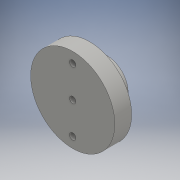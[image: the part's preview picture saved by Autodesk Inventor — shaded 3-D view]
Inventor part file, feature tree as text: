
AUTODESK INVENTOR PART (.ipt)
format: ipt  version: 2016 (Build 200138000, 138)  size: 136,704 bytes
history: native  units: in
note: dims shown in document units (in); Inventor stores cm internally (conversion verified against a paired STEP export)
features: sketch x3, extrude x2, plane x1
ambient origin geometry x8: Origin, YZ Plane, XZ Plane, XY Plane, X Axis, Y Axis, Z Axis, Center Point
bodies: Solid1 (feature_tree)
feature tree (6):
  extrude  "Extrusion1"  Depth=0.2in TaperAngle=0.0deg
  extrude  "Extrusion2"  Depth=0.184in
  plane  "Work Plane1"
  sketch  "Sketch5"  dims[d22=0.266in d23=0.098in d24=0.098in d25=0.5in d26=0.075in d27=1.0in d28=0.075in d29=0.075in d30=0.1384in d31=0.1384in d32=0.0108in d33=0.092in d34=0.0054in d35=0.092in]
  sketch  "Sketch1"  dims[d10=0.21in d11=0.0in d16=0.2in d17=0.0in]
  sketch  "Sketch2"  dims[d18=2.0in d21=0.184in]
